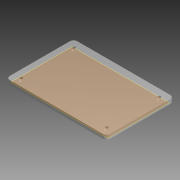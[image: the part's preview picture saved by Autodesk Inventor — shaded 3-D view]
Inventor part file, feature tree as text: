
AUTODESK INVENTOR PART (.ipt)
format: ipt  version: 2013 SP2 (Build 170200200, 200)  size: 107,520 bytes
history: native  units: mm
features: reference x4, plane x1, extrude x1, sketch x1
ambient origin geometry x8: Origin, YZ Plane, XZ Plane, XY Plane, X Axis, Y Axis, Z Axis, Center Point
bodies: Solid1 (feature_tree)
feature tree (7):
  plane  "Work Plane1"
  extrude  "Extrusion1"  Depth=110.0mm
  sketch  "Sketch1"  dims[d0=74.0mm d2=110.0mm d3=4.0mm d4=4.7mm d5=0.0mm]
  reference  "Reference1"
  reference  "Reference2"
  reference  "Reference3"
  reference  "Reference4"
